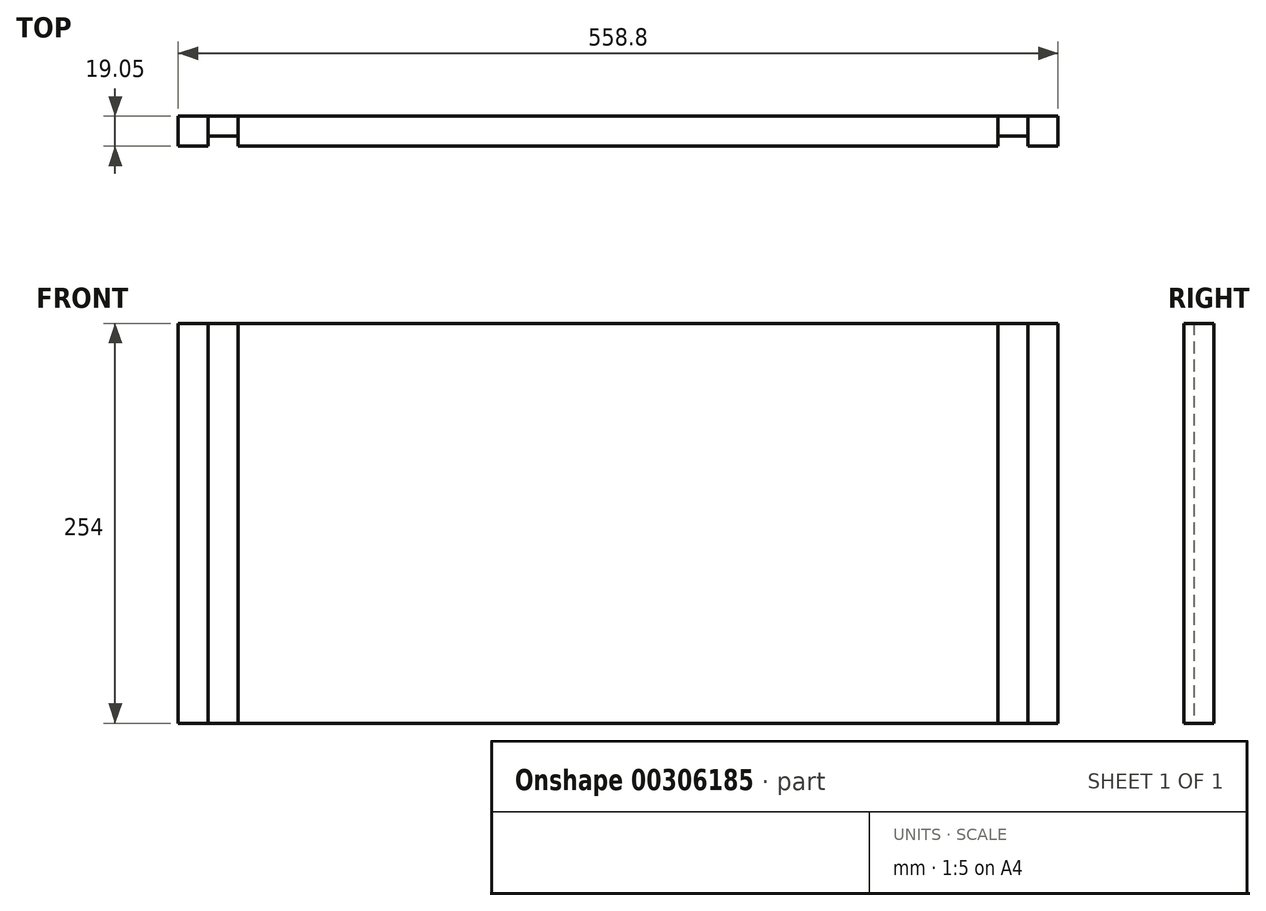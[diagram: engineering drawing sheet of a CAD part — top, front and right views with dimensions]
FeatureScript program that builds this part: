
annotation { "Feature Type Name" : "Feature", "Feature Type Description" : "" }
export const myFeature = defineFeature(function(context is Context, id is Id, definition is map)
    precondition{}
    {
        {
            var Q0;
            Q0=qCreatedBy(makeId("Front.planeOp"),FACE);
            var sketch = newSketch(context, id + "F0", { "sketchPlane" : qUnion([Q0])});
            skLineSegment(sketch, "E0.bottom", {"start": v(279.4, 127) * mm, "end": v(-279.4, 127) * mm});
            skLineSegment(sketch, "E0.top", {"start": v(279.4, -127) * mm, "end": v(-279.4, -127) * mm});
            skLineSegment(sketch, "E0.left", {"start": v(279.4, 127) * mm, "end": v(279.4, -127) * mm});
            skLineSegment(sketch, "E0.right", {"start": v(-279.4, 127) * mm, "end": v(-279.4, -127) * mm});
            skPoint(sketch, "E0.middle", {"position": v(0, 0) * mm});
            skLineSegment(sketch, "E1", {"start": v(0, 127) * mm, "end": v(0, -127) * mm});
            skLineSegment(sketch, "E2", {"start": v(-260.35, 127) * mm, "end": v(-260.35, -127) * mm});
            skLineSegment(sketch, "E3", {"start": v(-241.3, 127) * mm, "end": v(-241.3, -127) * mm});
            skLineSegment(sketch, "E4.MirrorCS", {"start": v(260.35, 127) * mm, "end": v(260.35, -127) * mm});
            skLineSegment(sketch, "E5.MirrorCS", {"start": v(241.3, 127) * mm, "end": v(241.3, -127) * mm});
            skSolve(sketch);
        }
        {
            var Q0;
            {var subQ0=sQuery(id+"F0.wireOp",EDGE,"E0.right");Q0=makeQuery(id+"F0.imprint","IMPRINT",FACE,{"disambiguationData":[TD([[makeQuery(id+"F0.imprint","IMPRINT",EDGE,{"derivedFrom":subQ0}),1.0]])]});}
            var Q1;
            {var subQ0=sQuery(id+"F0.wireOp",EDGE,"E1");Q1=makeQuery(id+"F0.imprint","IMPRINT",FACE,{"disambiguationData":[TD([[makeQuery(id+"F0.imprint","IMPRINT",EDGE,{"derivedFrom":subQ0}),-1.0]])]});}
            var Q2;
            {var subQ0=sQuery(id+"F0.wireOp",EDGE,"E0.left");Q2=makeQuery(id+"F0.imprint","IMPRINT",FACE,{"disambiguationData":[TD([[makeQuery(id+"F0.imprint","IMPRINT",EDGE,{"derivedFrom":subQ0}),-1.0]])]});}
            var Q3;
            {var subQ0=sQuery(id+"F0.wireOp",EDGE,"E1");Q3=makeQuery(id+"F0.imprint","IMPRINT",FACE,{"disambiguationData":[TD([[makeQuery(id+"F0.imprint","IMPRINT",EDGE,{"derivedFrom":subQ0}),1.0]])]});}
            extrude(context, id + "F1", {"entities" : qUnion([Q0, Q1, Q2, Q3]), "depth" : 19.05 * mm});
        }
        {
            var Q0;
            {var subQ0=sQuery(id+"F0.wireOp",EDGE,"E2");Q0=makeQuery(id+"F0.imprint","IMPRINT",FACE,{"disambiguationData":[TD([[makeQuery(id+"F0.imprint","IMPRINT",EDGE,{"derivedFrom":subQ0}),1.0]])]});}
            var Q1;
            {var subQ0=sQuery(id+"F0.wireOp",EDGE,"E4.MirrorCS");Q1=makeQuery(id+"F0.imprint","IMPRINT",FACE,{"disambiguationData":[TD([[makeQuery(id+"F0.imprint","IMPRINT",EDGE,{"derivedFrom":subQ0}),-1.0]])]});}
            extrude(context, id + "F2", {"entities" : qUnion([Q0, Q1]), "depth" : 12.7 * mm});
        }
    });
